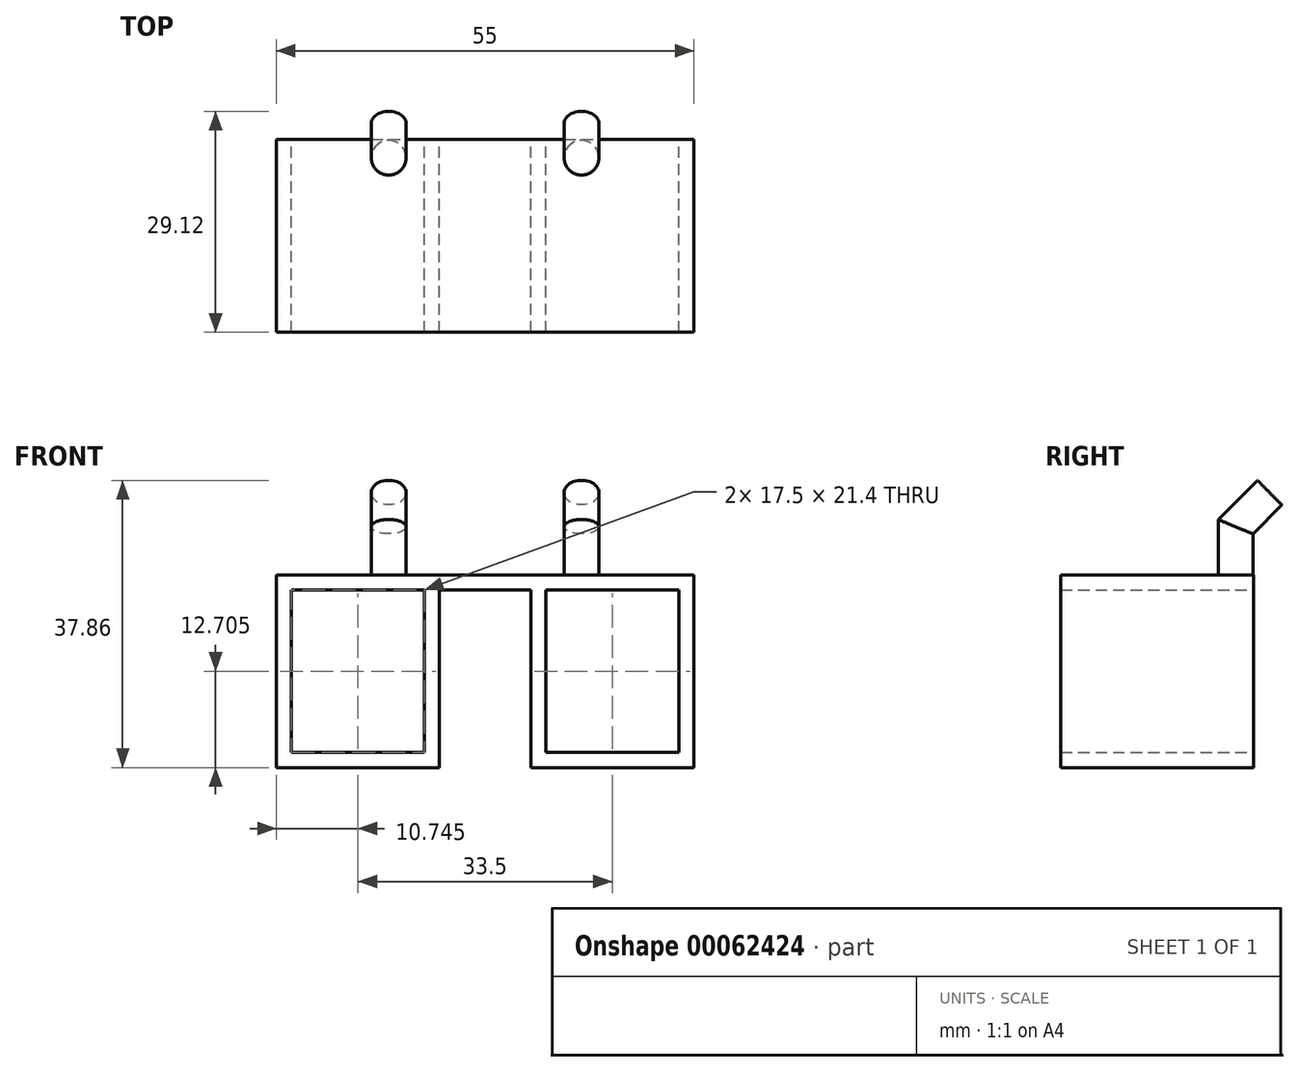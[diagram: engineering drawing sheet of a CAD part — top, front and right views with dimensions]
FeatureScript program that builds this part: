
annotation { "Feature Type Name" : "Feature", "Feature Type Description" : "" }
export const myFeature = defineFeature(function(context is Context, id is Id, definition is map)
    precondition{}
    {
        {
            var Q0;
            Q0=qCreatedBy(makeId("Top.planeOp"),FACE);
            var sketch = newSketch(context, id + "F0", { "sketchPlane" : qUnion([Q0])});
            skLineSegment(sketch, "E0.bottom", {"start": v(0, 0) * mm, "end": v(31.75, 0) * mm});
            skLineSegment(sketch, "E0.top", {"start": v(0, 9.52) * mm, "end": v(31.75, 9.52) * mm});
            skLineSegment(sketch, "E0.left", {"start": v(0, 0) * mm, "end": v(0, 9.52) * mm});
            skLineSegment(sketch, "E0.right", {"start": v(31.75, 0) * mm, "end": v(31.75, 9.52) * mm});
            skSolve(sketch);
        }
        {
            var Q0;
            Q0=makeQuery(id+"F0.imprint","IMPRINT",FACE,{"disambiguationData":[TD([[makeQuery(id+"F0.imprint","IMPRINT",EDGE,{"derivedFrom":sQuery(id+"F0.wireOp",EDGE,"E0.bottom")}),1.0]])]});
            extrude(context, id + "F1", {"entities" : qUnion([Q0]), "depth" : 3.17 * mm});
        }
        {
            var Q0;
            Q0=makeQuery(id+"F1.opExtrude","SWEPT_FACE",FACE,{"disambiguationData":[OSD([sQuery(id+"F0.wireOp",EDGE,"E0.right")])]});
            cPlane(context, id + "F2", {"entities" : qUnion([Q0]), "cplaneType" : CPlaneType.OFFSET, "offset" : 3.17 * mm, "oppositeDirection" : true, "width" : 152.4 * mm, "height" : 152.4 * mm});
        }
        {
            var Q0;
            Q0=qCreatedBy(id+"F2.planeOp",FACE);
            var sketch = newSketch(context, id + "F3", { "sketchPlane" : qUnion([Q0])});
            skLineSegment(sketch, "E1", {"start": v(7.14, 3.18) * mm, "end": v(7.14, 9.53) * mm});
            skLineSegment(sketch, "E2", {"start": v(7.14, 9.53) * mm, "end": v(11.63, 14.02) * mm});
            skSolve(sketch);
        }
        {
            var Q0;
            Q0=makeQuery(id+"F1.opExtrude","CAP_FACE",FACE,{"disambiguationData":[OSD([sQuery(id+"F0.wireOp",EDGE,"E0.bottom"),sQuery(id+"F0.wireOp",EDGE,"E0.top"),sQuery(id+"F0.wireOp",EDGE,"E0.left"),sQuery(id+"F0.wireOp",EDGE,"E0.right")])],"isStart":false});
            var sketch = newSketch(context, id + "F4", { "sketchPlane" : qUnion([Q0])});
            skCircle(sketch, "E3", {"center": v(28.57, 7.14) * mm, "radius": 2.29 * mm});
            skSolve(sketch);
        }
        {
            var Q0;
            Q0=makeQuery(id+"F4.imprint","IMPRINT",FACE,{"disambiguationData":[TD([[makeQuery(id+"F4.imprint","IMPRINT",EDGE,{"derivedFrom":sQuery(id+"F4.wireOp",EDGE,"E3")}),1.0]])]});
            var Q1;
            Q1=sQuery(id+"F3.wireOp",EDGE,"E1");
            var Q2;
            Q2=sQuery(id+"F3.wireOp",EDGE,"E2");
            sweep(context, id + "F5", {"operationType" : NewBodyOperationType.ADD, "profiles" : qUnion([Q0]), "path" : qUnion([Q1, Q2])});
        }
        {
            var Q0;
            Q0=qCreatedBy(id+"F2.planeOp",FACE);
            cPlane(context, id + "F6", {"entities" : qUnion([Q0]), "cplaneType" : CPlaneType.OFFSET, "offset" : 25.4 * mm, "oppositeDirection" : true, "width" : 152.4 * mm, "height" : 152.4 * mm});
        }
        {
            var Q0;
            Q0=qCreatedBy(id+"F6.planeOp",FACE);
            var sketch = newSketch(context, id + "F7", { "sketchPlane" : qUnion([Q0])});
            skLineSegment(sketch, "E4.0", {"start": v(7.14, 3.18) * mm, "end": v(7.14, 9.53) * mm});
            skLineSegment(sketch, "E4.1", {"start": v(7.14, 9.53) * mm, "end": v(11.63, 14.02) * mm});
            skSolve(sketch);
        }
        {
            var Q0;
            Q0=makeQuery(id+"F1.opExtrude","CAP_FACE",FACE,{"disambiguationData":[OSD([sQuery(id+"F0.wireOp",EDGE,"E0.bottom"),sQuery(id+"F0.wireOp",EDGE,"E0.top"),sQuery(id+"F0.wireOp",EDGE,"E0.left"),sQuery(id+"F0.wireOp",EDGE,"E0.right")])],"isStart":false});
            var sketch = newSketch(context, id + "F8", { "sketchPlane" : qUnion([Q0])});
            skCircle(sketch, "E5", {"center": v(3.17, 7.14) * mm, "radius": 2.29 * mm});
            skSolve(sketch);
        }
        {
            var Q0;
            Q0=makeQuery(id+"F8.imprint","IMPRINT",FACE,{"disambiguationData":[TD([[makeQuery(id+"F8.imprint","IMPRINT",EDGE,{"derivedFrom":sQuery(id+"F8.wireOp",EDGE,"E5")}),1.0]])]});
            var Q1;
            Q1=sQuery(id+"F7.wireOp",EDGE,"E4.0");
            var Q2;
            Q2=sQuery(id+"F7.wireOp",EDGE,"E4.1");
            sweep(context, id + "F9", {"operationType" : NewBodyOperationType.ADD, "profiles" : qUnion([Q0]), "path" : qUnion([Q1, Q2])});
        }
        {
            var Q0;
            Q0=makeQuery(id+"F1.opExtrude","CAP_FACE",FACE,{"disambiguationData":[OSD([sQuery(id+"F0.wireOp",EDGE,"E0.bottom"),sQuery(id+"F0.wireOp",EDGE,"E0.top"),sQuery(id+"F0.wireOp",EDGE,"E0.left"),sQuery(id+"F0.wireOp",EDGE,"E0.right")])],"isStart":false});
            var sketch = newSketch(context, id + "F10", { "sketchPlane" : qUnion([Q0])});
            skLineSegment(sketch, "E6.bottom", {"start": v(-11.62, 9.52) * mm, "end": v(43.38, 9.52) * mm});
            skLineSegment(sketch, "E6.top", {"start": v(-11.62, -15.88) * mm, "end": v(43.38, -15.88) * mm});
            skLineSegment(sketch, "E6.left", {"start": v(-11.62, 9.52) * mm, "end": v(-11.62, -15.88) * mm});
            skLineSegment(sketch, "E6.right", {"start": v(43.38, 9.53) * mm, "end": v(43.38, -15.88) * mm});
            skLineSegment(sketch, "E7", {"start": v(15.88, 0) * mm, "end": v(15.88, -15.88) * mm, "construction": true});
            skSolve(sketch);
        }
        {
            var Q0;
            Q0 = qSketchRegion(id + "F10", true);
            extrude(context, id + "F11", {"entities" : qUnion([Q0]), "operationType" : NewBodyOperationType.ADD, "oppositeDirection" : true, "depth" : 25.4 * mm});
        }
        {
            var Q0;
            Q0=makeQuery(id+"F11.boolean.opBoolean","MERGE",FACE,{"derivedFrom":[makeQuery(id+"F1.opExtrude","SWEPT_FACE",FACE,{"disambiguationData":[OSD([sQuery(id+"F0.wireOp",EDGE,"E0.top")])]}),makeQuery(id+"F11.opExtrude","SWEPT_FACE",FACE,{"disambiguationData":[OSD([sQuery(id+"F10.wireOp",EDGE,"E6.bottom")])]})]});
            var sketch = newSketch(context, id + "F12", { "sketchPlane" : qUnion([Q0])});
            skLineSegment(sketch, "E8.bottom", {"start": v(-21.88, -22.23) * mm, "end": v(-9.87, -22.23) * mm});
            skLineSegment(sketch, "E8.top", {"start": v(-21.88, 1.17) * mm, "end": v(-9.88, 1.18) * mm});
            skLineSegment(sketch, "E8.left", {"start": v(-21.88, -22.23) * mm, "end": v(-21.88, 1.17) * mm});
            skLineSegment(sketch, "E8.right", {"start": v(-9.87, -22.23) * mm, "end": v(-9.88, 1.17) * mm});
            skLineSegment(sketch, "E9", {"start": v(-15.88, 1.18) * mm, "end": v(-15.88, 3.18) * mm, "construction": true});
            skLineSegment(sketch, "E10.bottom", {"start": v(-41.37, -20.23) * mm, "end": v(-23.87, -20.22) * mm});
            skLineSegment(sketch, "E10.top", {"start": v(-41.37, 1.17) * mm, "end": v(-23.88, 1.17) * mm});
            skLineSegment(sketch, "E10.left", {"start": v(-41.37, -20.23) * mm, "end": v(-41.37, 1.17) * mm});
            skLineSegment(sketch, "E10.right", {"start": v(-23.88, -20.23) * mm, "end": v(-23.88, 1.17) * mm});
            skLineSegment(sketch, "E11.bottom", {"start": v(9.63, -20.22) * mm, "end": v(-7.87, -20.23) * mm});
            skLineSegment(sketch, "E11.top", {"start": v(9.62, 1.18) * mm, "end": v(-7.88, 1.17) * mm});
            skLineSegment(sketch, "E11.left", {"start": v(9.62, -20.22) * mm, "end": v(9.62, 1.18) * mm});
            skLineSegment(sketch, "E11.right", {"start": v(-7.88, -20.23) * mm, "end": v(-7.88, 1.17) * mm});
            skSolve(sketch);
        }
        {
            var Q0;
            Q0=makeQuery(id+"F12.imprint","IMPRINT",FACE,{"disambiguationData":[TD([[makeQuery(id+"F12.imprint","IMPRINT",EDGE,{"derivedFrom":sQuery(id+"F12.wireOp",EDGE,"E10.bottom")}),1.0]])]});
            var Q1;
            Q1=makeQuery(id+"F12.imprint","IMPRINT",FACE,{"disambiguationData":[TD([[makeQuery(id+"F12.imprint","IMPRINT",EDGE,{"derivedFrom":sQuery(id+"F12.wireOp",EDGE,"E8.bottom")}),-1.0]])]});
            var Q2;
            Q2=makeQuery(id+"F12.imprint","IMPRINT",FACE,{"disambiguationData":[TD([[makeQuery(id+"F12.imprint","IMPRINT",EDGE,{"derivedFrom":sQuery(id+"F12.wireOp",EDGE,"E11.bottom")}),-1.0]])]});
            extrude(context, id + "F13", {"entities" : qUnion([Q0, Q1, Q2]), "operationType" : NewBodyOperationType.REMOVE, "endBound" : BoundingType.THROUGH_ALL, "oppositeDirection" : true, "depth" : 25.4 * mm});
        }
    });
